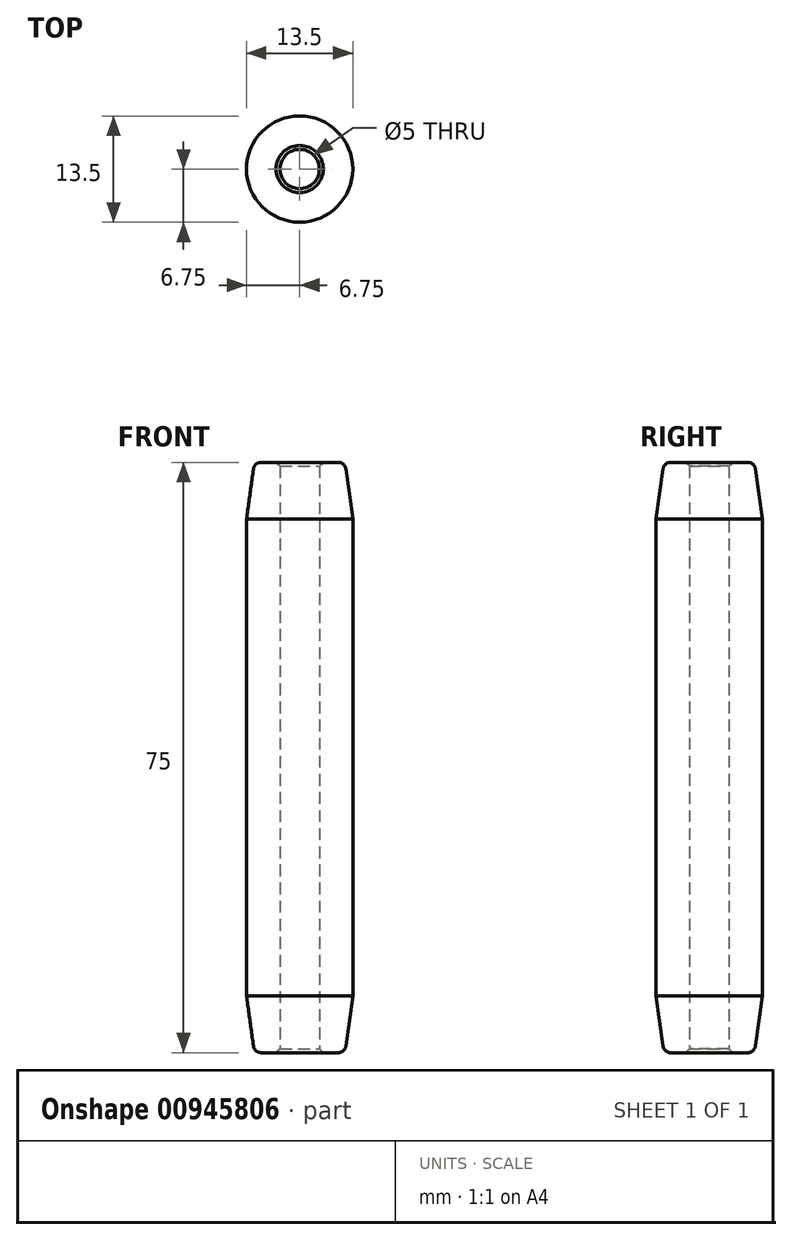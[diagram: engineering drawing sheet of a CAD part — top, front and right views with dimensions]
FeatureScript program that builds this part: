
annotation { "Feature Type Name" : "Feature", "Feature Type Description" : "" }
export const myFeature = defineFeature(function(context is Context, id is Id, definition is map)
    precondition{}
    {
        {
            var Q0;
            Q0=qCreatedBy(makeId("Front.planeOp"),FACE);
            var sketch = newSketch(context, id + "F0", { "sketchPlane" : qUnion([Q0])});
            skLineSegment(sketch, "E0", {"start": v(2.5, 37.5) * mm, "end": v(2.5, -37.5) * mm});
            skLineSegment(sketch, "E1", {"start": v(2.5, -37.5) * mm, "end": v(5.75, -37.5) * mm});
            skLineSegment(sketch, "E2", {"start": v(5.75, -37.5) * mm, "end": v(6.75, -30.3) * mm});
            skLineSegment(sketch, "E3", {"start": v(6.75, -30.3) * mm, "end": v(6.75, 30.3) * mm});
            skLineSegment(sketch, "E4", {"start": v(2.5, 37.5) * mm, "end": v(5.75, 37.5) * mm});
            skLineSegment(sketch, "E5", {"start": v(5.75, 37.5) * mm, "end": v(6.75, 30.3) * mm});
            skLineSegment(sketch, "E6", {"start": v(2.5, 37.5) * mm, "end": v(0, 37.5) * mm});
            skLineSegment(sketch, "E7", {"start": v(2.5, -37.5) * mm, "end": v(0, -37.5) * mm});
            skLineSegment(sketch, "E8", {"start": v(0, -37.5) * mm, "end": v(0, 37.5) * mm});
            skSolve(sketch);
        }
        {
            var Q0;
            Q0=makeQuery(id+"F0.imprint","IMPRINT",FACE,{"disambiguationData":[TD([[makeQuery(id+"F0.imprint","IMPRINT",EDGE,{"derivedFrom":sQuery(id+"F0.wireOp",EDGE,"E0")}),1.0]])]});
            var Q1;
            Q1=sQuery(id+"F0.wireOp",EDGE,"E8");
            revolve(context, id + "F1", {"surfaceOperationType" : NewSurfaceOperationType.NEW, "entities" : qUnion([Q0]), "axis" : qUnion([Q1]), "revolveType" : RevolveType.FULL});
        }
        {
            var Q0;
            Q0=makeQuery(id+"F1.opRevolve","SWEPT_EDGE",EDGE,{"disambiguationData":[OSD([sQuery(id+"F0.wireOp",EDGE,"E4"),sQuery(id+"F0.wireOp",EDGE,"E5")])]});
            var Q1;
            Q1=makeQuery(id+"F1.opRevolve","SWEPT_EDGE",EDGE,{"disambiguationData":[OSD([sQuery(id+"F0.wireOp",EDGE,"E1"),sQuery(id+"F0.wireOp",EDGE,"E2")])]});
            fillet(context, id + "F2", {"entities" : qUnion([Q0, Q1]), "radius" : 1 * mm, "tangentPropagation" : true, "allowEdgeOverflow" : false});
        }
        {
            var Q0;
            Q0=makeQuery(id+"F1.opRevolve","SWEPT_EDGE",EDGE,{"disambiguationData":[OSD([sQuery(id+"F0.wireOp",EDGE,"E0"),sQuery(id+"F0.wireOp",EDGE,"E4"),sQuery(id+"F0.wireOp",EDGE,"E6")])]});
            var Q1;
            Q1=makeQuery(id+"F1.opRevolve","SWEPT_EDGE",EDGE,{"disambiguationData":[OSD([sQuery(id+"F0.wireOp",EDGE,"E0"),sQuery(id+"F0.wireOp",EDGE,"E1"),sQuery(id+"F0.wireOp",EDGE,"E7")])]});
            chamfer(context, id + "F3", {"entities" : qUnion([Q0, Q1]), "width" : 0.5 * mm, "tangentPropagation" : true});
        }
    });
